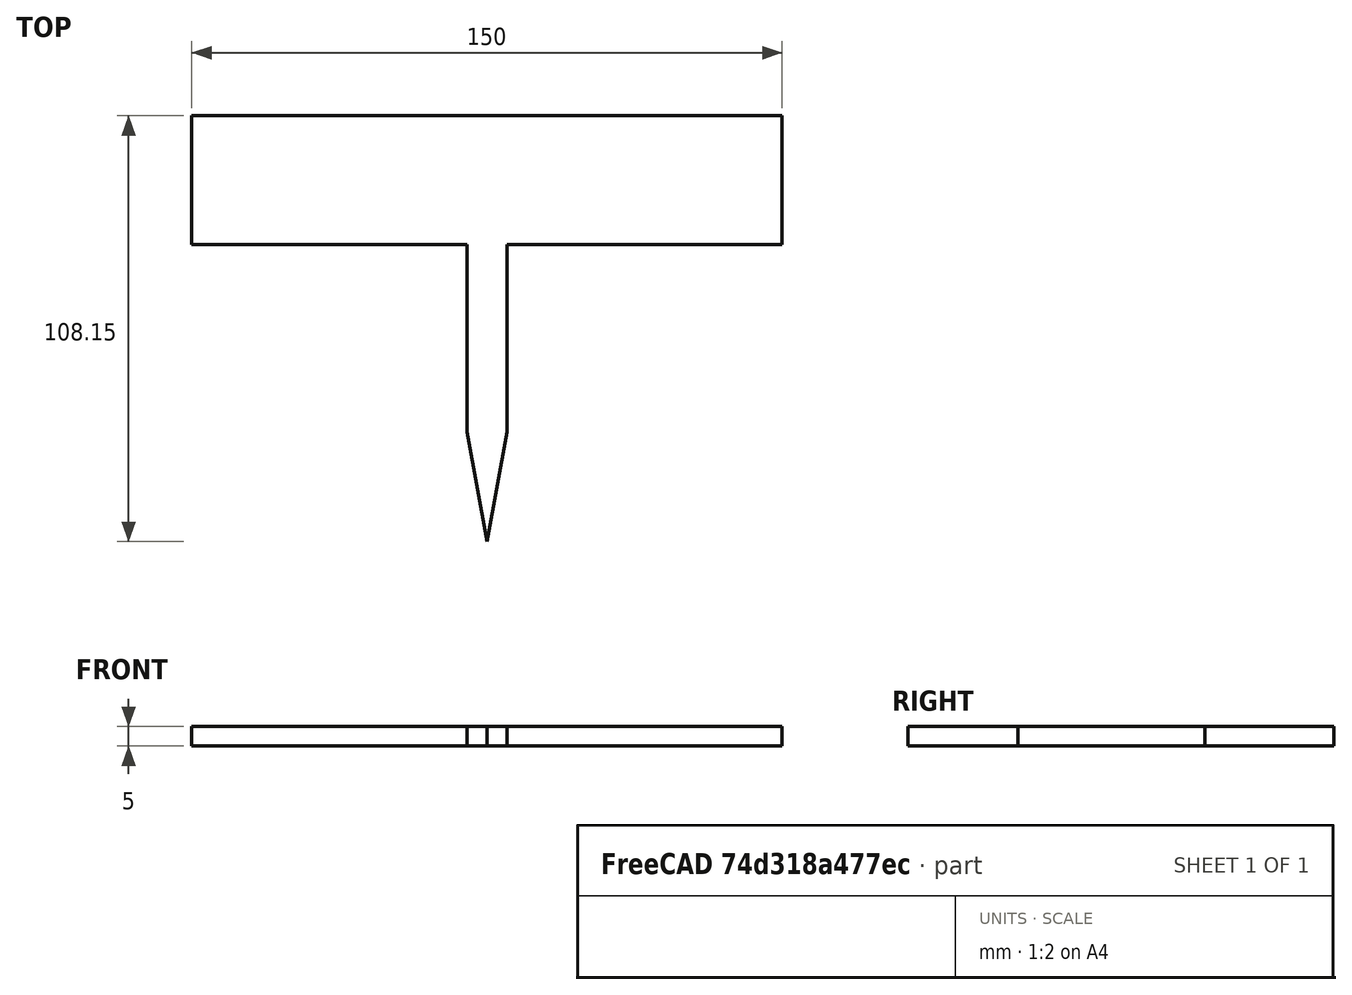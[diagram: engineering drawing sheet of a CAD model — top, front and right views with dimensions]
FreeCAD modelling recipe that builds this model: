
FCSTD DOCUMENT  (FreeCAD 0.14R3702 (Git))
Label: cartel_huerto
License: CC-BY 3.0
LicenseURL: http://creativecommons.org/licenses/by/3.0/
objects: Sketcher::SketchObject×1, PartDesign::Pad×1
note: 3 computed .brp shape members not serialized (recipe doc carries the construction recipe); baked Part::Feature solids carry a one-line shape summary decoded from their .brp

FEATURE [Sketcher::SketchObject] Sketch
  sketch-geometry (9):
    g0: LineSegment StartX=-75 StartY=16.3423 StartZ=0 EndX=75 EndY=16.3423 EndZ=0
    g1: LineSegment StartX=75 StartY=16.3423 StartZ=0 EndX=75 EndY=-16.3423 EndZ=0
    g2: LineSegment StartX=75 StartY=-16.3423 StartZ=0 EndX=5.09593 EndY=-16.3423 EndZ=0
    g3: LineSegment StartX=5.09593 StartY=-16.3423 StartZ=0 EndX=5.09593 EndY=-63.9541 EndZ=0
    g4: LineSegment StartX=5.09593 StartY=-63.9541 StartZ=0 EndX=0 EndY=-91.8105 EndZ=0
    g5: LineSegment StartX=0 StartY=-91.8105 StartZ=0 EndX=-5.09593 EndY=-63.9541 EndZ=0
    g6: LineSegment StartX=-5.09593 StartY=-63.9541 StartZ=0 EndX=-5.09593 EndY=-16.3423 EndZ=0
    g7: LineSegment StartX=-5.09593 StartY=-16.3423 StartZ=0 EndX=-75 EndY=-16.3423 EndZ=0
    g8: LineSegment StartX=-75 StartY=-16.3423 StartZ=0 EndX=-75 EndY=16.3423 EndZ=0
  constraints (22):
    c: Horizontal(g0)
    c: Coincident(g0,g1)
    c: Vertical(g1)
    c: Coincident(g1,g2)
    c: Horizontal(g2)
    c: Coincident(g2,g3)
    c: Vertical(g3)
    c: Coincident(g3,g4)
    c: PointOnObject(g4,g-2)
    c: Coincident(g4,g5)
    c: Coincident(g5,g6)
    c: Vertical(g6)
    c: Coincident(g6,g7)
    c: Coincident(g7,g8)
    c: Vertical(g8)
    c: Coincident(g0,g8)
    c: Symmetric(g2,g6,g-2)
    c: Horizontal(g7)
    c: Symmetric(g5,g3,g-2)
    c: Symmetric(g0,g7,g-1)
    c: Symmetric(g0,g0,g-2)
    c: Distance(g0) = 150
FEATURE [PartDesign::Pad] Pad
  Length = 5
  Length2 = 100
  Sketch = -> Sketch
  Type = 0
